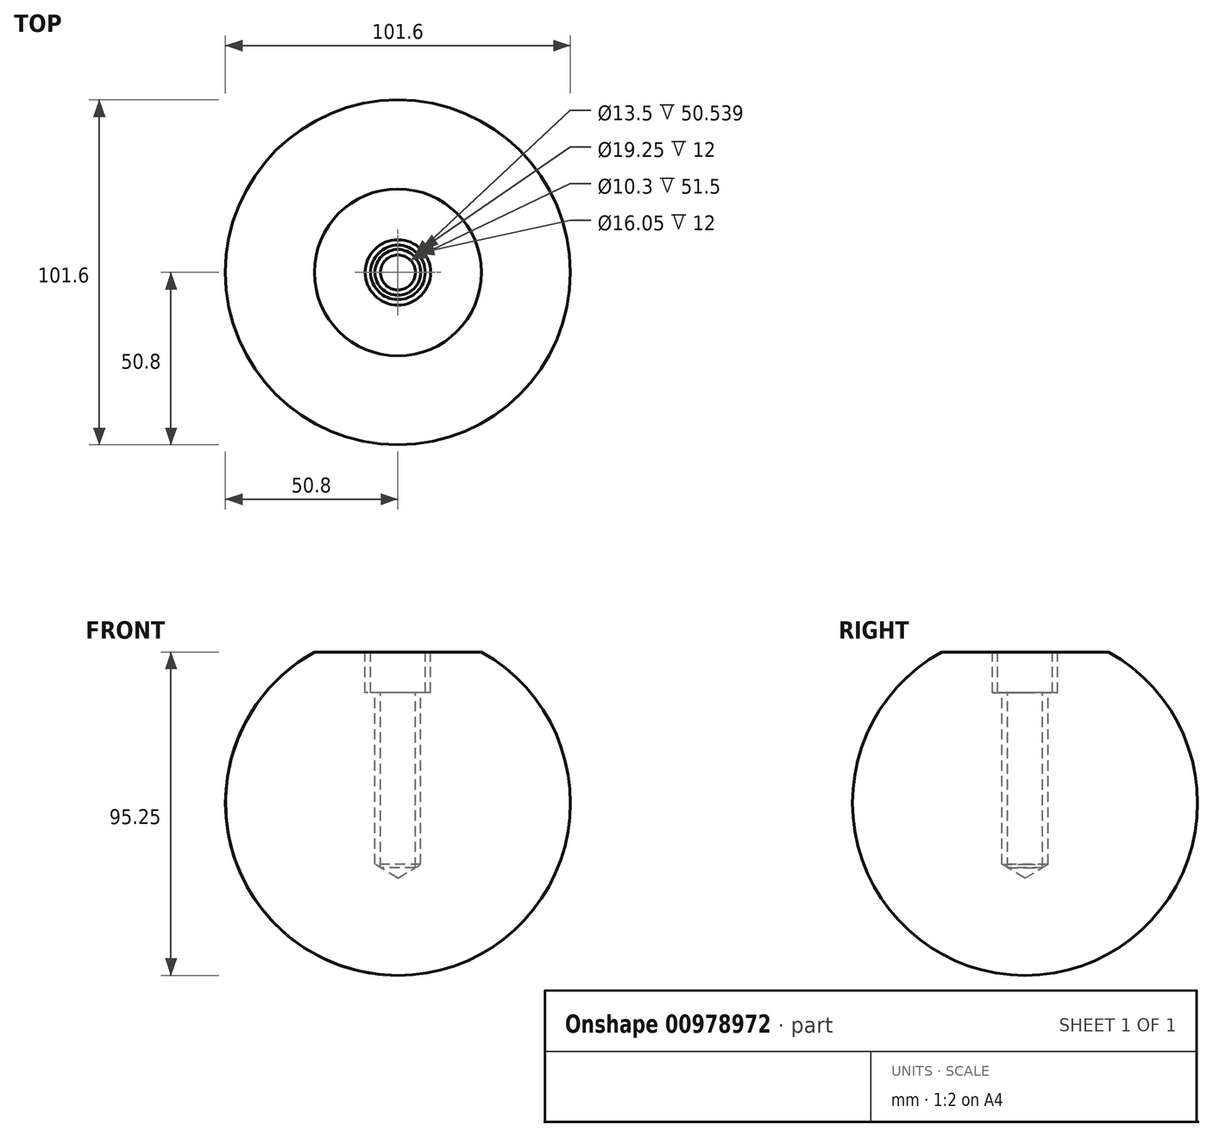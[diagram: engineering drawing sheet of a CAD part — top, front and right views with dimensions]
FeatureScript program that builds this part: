
annotation { "Feature Type Name" : "Feature", "Feature Type Description" : "" }
export const myFeature = defineFeature(function(context is Context, id is Id, definition is map)
    precondition{}
    {
        {
            var Q0;
            Q0=qCreatedBy(makeId("Front.planeOp"),FACE);
            var sketch = newSketch(context, id + "F0", { "sketchPlane" : qUnion([Q0])});
            skArc(sketch, "E0", {"start": v(0, -50.8) * mm, "mid": v(50.8, 0) * mm, "end": v(0, 50.8) * mm});
            skLineSegment(sketch, "E1", {"start": v(0, 50.8) * mm, "end": v(0, -50.8) * mm});
            skSolve(sketch);
        }
        {
            var Q0;
            Q0=makeQuery(id+"F0.imprint","IMPRINT",FACE,{"disambiguationData":[TD([[makeQuery(id+"F0.imprint","IMPRINT",EDGE,{"derivedFrom":sQuery(id+"F0.wireOp",EDGE,"E0")}),1.0]])]});
            var Q1;
            Q1=sQuery(id+"F0.wireOp",EDGE,"E1");
            revolve(context, id + "F1", {"surfaceOperationType" : NewSurfaceOperationType.NEW, "entities" : qUnion([Q0]), "axis" : qUnion([Q1]), "revolveType" : RevolveType.FULL});
        }
        {
            var Q0;
            Q0=makeQuery(id+"F0.imprint","IMPRINT",FACE,{"disambiguationData":[TD([[makeQuery(id+"F0.imprint","IMPRINT",EDGE,{"derivedFrom":sQuery(id+"F0.wireOp",EDGE,"E0")}),1.0]])]});
            var Q1;
            Q1=sQuery(id+"F0.wireOp",EDGE,"E1");
            revolve(context, id + "F2", {"surfaceOperationType" : NewSurfaceOperationType.NEW, "entities" : qUnion([Q0]), "axis" : qUnion([Q1]), "revolveType" : RevolveType.FULL});
        }
        {
            var Q0;
            Q0=qCreatedBy(makeId("Top.planeOp"),FACE);
            cPlane(context, id + "F3", {"entities" : qUnion([Q0]), "cplaneType" : CPlaneType.OFFSET, "offset" : 44.45 * mm, "width" : 152.4 * mm, "height" : 152.4 * mm});
        }
        {
            var Q0;
            Q0=qCreatedBy(id+"F3.planeOp",FACE);
            var sketch = newSketch(context, id + "F4", { "sketchPlane" : qUnion([Q0])});
            skPoint(sketch, "E2.middle", {"position": v(0, 0) * mm});
            skLineSegment(sketch, "E3.bottom", {"start": v(28.58, 28.58) * mm, "end": v(-28.57, 28.58) * mm});
            skLineSegment(sketch, "E3.top", {"start": v(28.58, -28.58) * mm, "end": v(-28.58, -28.58) * mm});
            skLineSegment(sketch, "E3.left", {"start": v(28.58, 28.58) * mm, "end": v(28.58, -28.58) * mm});
            skLineSegment(sketch, "E3.right", {"start": v(-28.57, 28.58) * mm, "end": v(-28.58, -28.58) * mm});
            skSolve(sketch);
        }
        {
            var Q0;
            Q0=makeQuery(id+"F4.imprint","IMPRINT",FACE,{"disambiguationData":[TD([[makeQuery(id+"F4.imprint","IMPRINT",EDGE,{"derivedFrom":sQuery(id+"F4.wireOp",EDGE,"E3.bottom")}),1.0]])]});
            extrude(context, id + "F5", {"entities" : qUnion([Q0]), "operationType" : NewBodyOperationType.REMOVE, "depth" : 14.73 * mm, "offsetDistance" : 25.4 * mm});
        }
        {
            var Q0;
            Q0=makeQuery(id+"F5.boolean.opBoolean","COPY",FACE,{"derivedFrom":makeQuery(id+"F5.opExtrude","CAP_FACE",FACE,{"disambiguationData":[OSD([sQuery(id+"F4.wireOp",EDGE,"E3.bottom"),sQuery(id+"F4.wireOp",EDGE,"E3.top"),sQuery(id+"F4.wireOp",EDGE,"E3.left"),sQuery(id+"F4.wireOp",EDGE,"E3.right")])],"isStart":true})});
            var sketch = newSketch(context, id + "F6", { "sketchPlane" : qUnion([Q0])});
            skCircle(sketch, "E4", {"center": v(0, 0) * mm, "radius": 9.63 * mm});
            skSolve(sketch);
        }
        {
            var Q0;
            Q0=sQuery(id+"F6.wireOp",VERTEX,"E4.center");
            var Q1;
            Q1=makeQuery(id+"F2.opRevolve","SWEPT_BODY",BODY,{"disambiguationData":[OSD([sQuery(id+"F0.wireOp",EDGE,"E0"),sQuery(id+"F0.wireOp",EDGE,"E1")])]});
            var Q2;
            Q2=makeQuery(id+"F1.opRevolve","SWEPT_BODY",BODY,{"disambiguationData":[OSD([sQuery(id+"F0.wireOp",EDGE,"E0"),sQuery(id+"F0.wireOp",EDGE,"E1")])]});
            hole(context, id + "F7", {"style" : HoleStyle.C_BORE, "endStyle" : HoleEndStyle.BLIND_IN_LAST, "holeDiameter" : 13.5 * mm, "cBoreDiameter" : 19.25 * mm, "cBoreDepth" : 12 * mm, "tapDrillDiameter" : 10.3 * mm, "majorDiameter" : 6.35 * mm, "holeDepth" : 63.5 * mm, "isTappedThrough" : true, "tappedDepth" : 12.7 * mm, "tapClearance" : 3, "locations" : qUnion([Q0]), "scope" : qUnion([Q1, Q2])});
        }
    });
